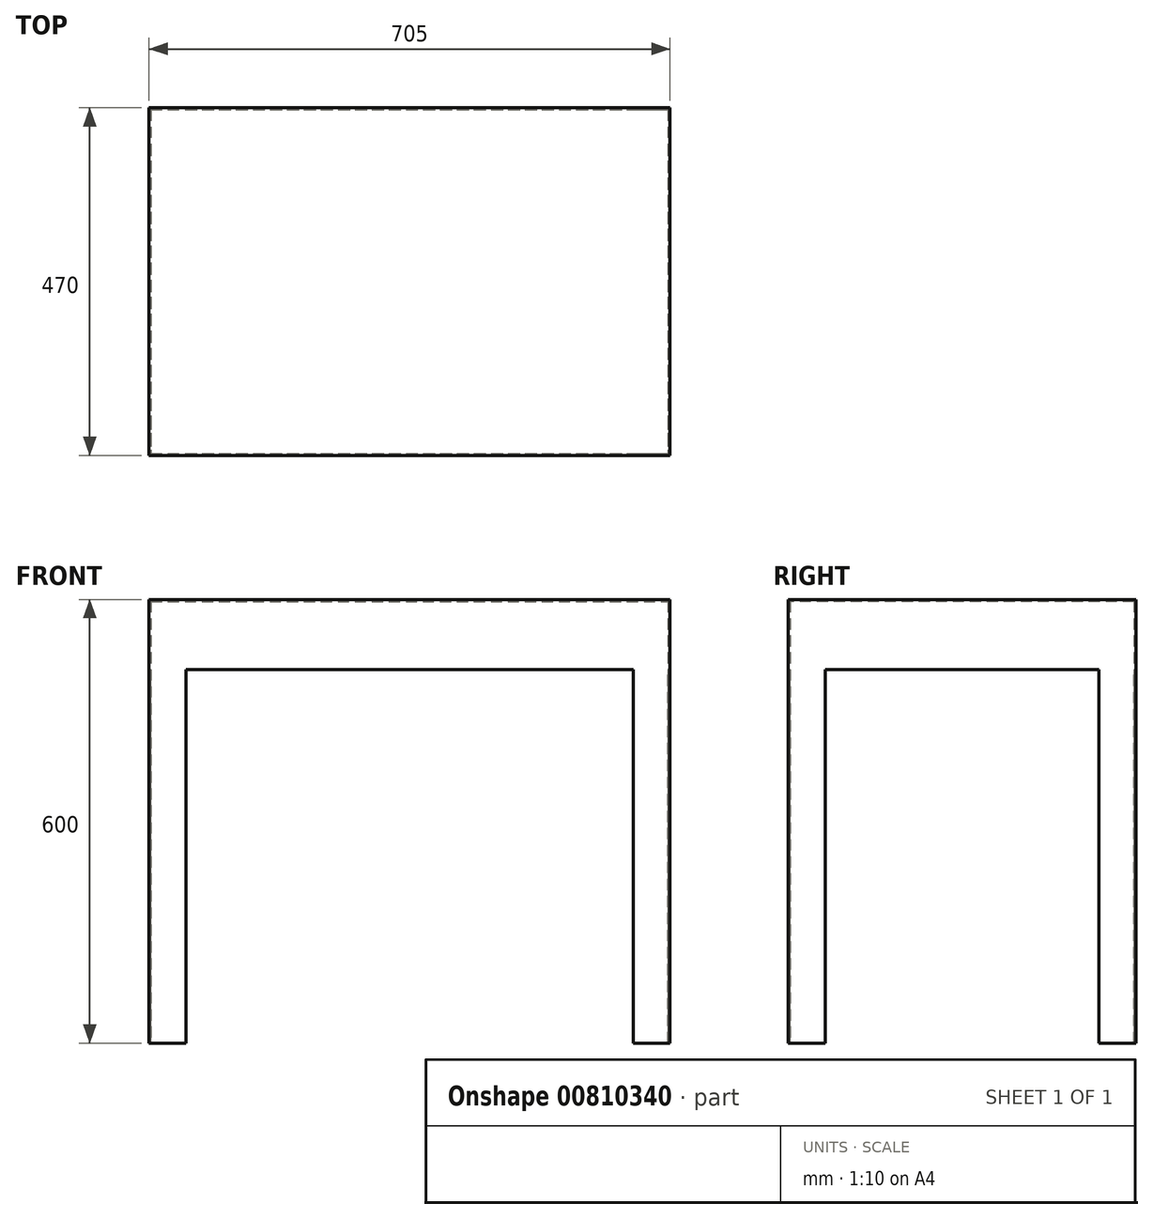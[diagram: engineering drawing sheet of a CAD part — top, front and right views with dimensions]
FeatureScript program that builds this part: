
annotation { "Feature Type Name" : "Feature", "Feature Type Description" : "" }
export const myFeature = defineFeature(function(context is Context, id is Id, definition is map)
    precondition{}
    {
        {
            var Q0;
            Q0=qCreatedBy(makeId("Top.planeOp"),FACE);
            var sketch = newSketch(context, id + "F0", { "sketchPlane" : qUnion([Q0])});
            skLineSegment(sketch, "E0.bottom", {"start": v(-352.5, 235) * mm, "end": v(352.5, 235) * mm});
            skLineSegment(sketch, "E0.top", {"start": v(-352.5, -235) * mm, "end": v(352.5, -235) * mm});
            skLineSegment(sketch, "E0.left", {"start": v(-352.5, 235) * mm, "end": v(-352.5, -235) * mm});
            skLineSegment(sketch, "E0.right", {"start": v(352.5, 235) * mm, "end": v(352.5, -235) * mm});
            skLineSegment(sketch, "E1", {"start": v(-574.07, 0) * mm, "end": v(586.89, 0) * mm, "construction": true});
            skLineSegment(sketch, "E2", {"start": v(0, 389.12) * mm, "end": v(0, -295.73) * mm, "construction": true});
            skSolve(sketch);
        }
        {
            var Q0;
            Q0 = qSketchRegion(id + "F0", true);
            extrude(context, id + "F1", {"entities" : qUnion([Q0]), "depth" : 95 * mm, "offsetDistance" : 25.4 * mm});
        }
        {
            var Q0;
            Q0=makeQuery(id+"F1.opExtrude","CAP_FACE",FACE,{"disambiguationData":[OSD([sQuery(id+"F0.wireOp",EDGE,"E0.bottom"),sQuery(id+"F0.wireOp",EDGE,"E0.top"),sQuery(id+"F0.wireOp",EDGE,"E0.left"),sQuery(id+"F0.wireOp",EDGE,"E0.right")])],"isStart":true});
            shell(context, id + "F2", {"entities" : qUnion([Q0]), "thickness" : 2.54 * mm});
        }
        {
            var Q0;
            Q0=makeQuery(id+"F1.opExtrude","CAP_FACE",FACE,{"disambiguationData":[OSD([sQuery(id+"F0.wireOp",EDGE,"E0.bottom"),sQuery(id+"F0.wireOp",EDGE,"E0.top"),sQuery(id+"F0.wireOp",EDGE,"E0.left"),sQuery(id+"F0.wireOp",EDGE,"E0.right")])],"isStart":true});
            var sketch = newSketch(context, id + "F3", { "sketchPlane" : qUnion([Q0])});
            skLineSegment(sketch, "E3", {"start": v(302.5, 235) * mm, "end": v(352.5, 235) * mm});
            skLineSegment(sketch, "E4", {"start": v(352.5, 235) * mm, "end": v(352.5, 185) * mm});
            skLineSegment(sketch, "E5", {"start": v(352.5, 185) * mm, "end": v(349.96, 185) * mm});
            skLineSegment(sketch, "E6", {"start": v(349.96, 185) * mm, "end": v(349.96, 232.46) * mm});
            skLineSegment(sketch, "E7", {"start": v(349.96, 232.46) * mm, "end": v(302.5, 232.46) * mm});
            skLineSegment(sketch, "E8", {"start": v(302.5, 232.46) * mm, "end": v(302.5, 235) * mm});
            skLineSegment(sketch, "E9", {"start": v(-352.5, 185) * mm, "end": v(-352.5, 235) * mm});
            skLineSegment(sketch, "E10", {"start": v(-352.5, 235) * mm, "end": v(-302.5, 235) * mm});
            skLineSegment(sketch, "E11", {"start": v(-302.5, 235) * mm, "end": v(-302.5, 232.46) * mm});
            skLineSegment(sketch, "E12", {"start": v(-302.5, 232.46) * mm, "end": v(-349.96, 232.46) * mm});
            skLineSegment(sketch, "E13", {"start": v(-349.96, 232.46) * mm, "end": v(-349.96, 185) * mm});
            skLineSegment(sketch, "E14", {"start": v(-349.96, 185) * mm, "end": v(-352.5, 185) * mm});
            skLineSegment(sketch, "E15", {"start": v(-352.5, -235) * mm, "end": v(-352.5, -185) * mm});
            skLineSegment(sketch, "E16", {"start": v(-352.5, -185) * mm, "end": v(-349.96, -185) * mm});
            skLineSegment(sketch, "E17", {"start": v(-349.96, -185) * mm, "end": v(-349.96, -232.46) * mm});
            skLineSegment(sketch, "E18", {"start": v(-349.96, -232.46) * mm, "end": v(-302.5, -232.46) * mm});
            skLineSegment(sketch, "E19", {"start": v(-302.5, -232.46) * mm, "end": v(-302.5, -235) * mm});
            skLineSegment(sketch, "E20", {"start": v(-302.5, -235) * mm, "end": v(-352.5, -235) * mm});
            skLineSegment(sketch, "E21", {"start": v(302.5, -235) * mm, "end": v(352.5, -235) * mm});
            skLineSegment(sketch, "E22", {"start": v(352.5, -235) * mm, "end": v(352.5, -185) * mm});
            skLineSegment(sketch, "E23", {"start": v(352.5, -185) * mm, "end": v(349.96, -185) * mm});
            skLineSegment(sketch, "E24", {"start": v(349.96, -185) * mm, "end": v(349.96, -232.46) * mm});
            skLineSegment(sketch, "E25", {"start": v(349.96, -232.46) * mm, "end": v(302.5, -232.46) * mm});
            skLineSegment(sketch, "E26", {"start": v(302.5, -232.46) * mm, "end": v(302.5, -235) * mm});
            skSolve(sketch);
        }
        {
            var Q0;
            Q0 = qSketchRegion(id + "F3", true);
            extrude(context, id + "F4", {"entities" : qUnion([Q0]), "operationType" : NewBodyOperationType.ADD, "depth" : 505 * mm, "offsetDistance" : 25.4 * mm});
        }
    });
